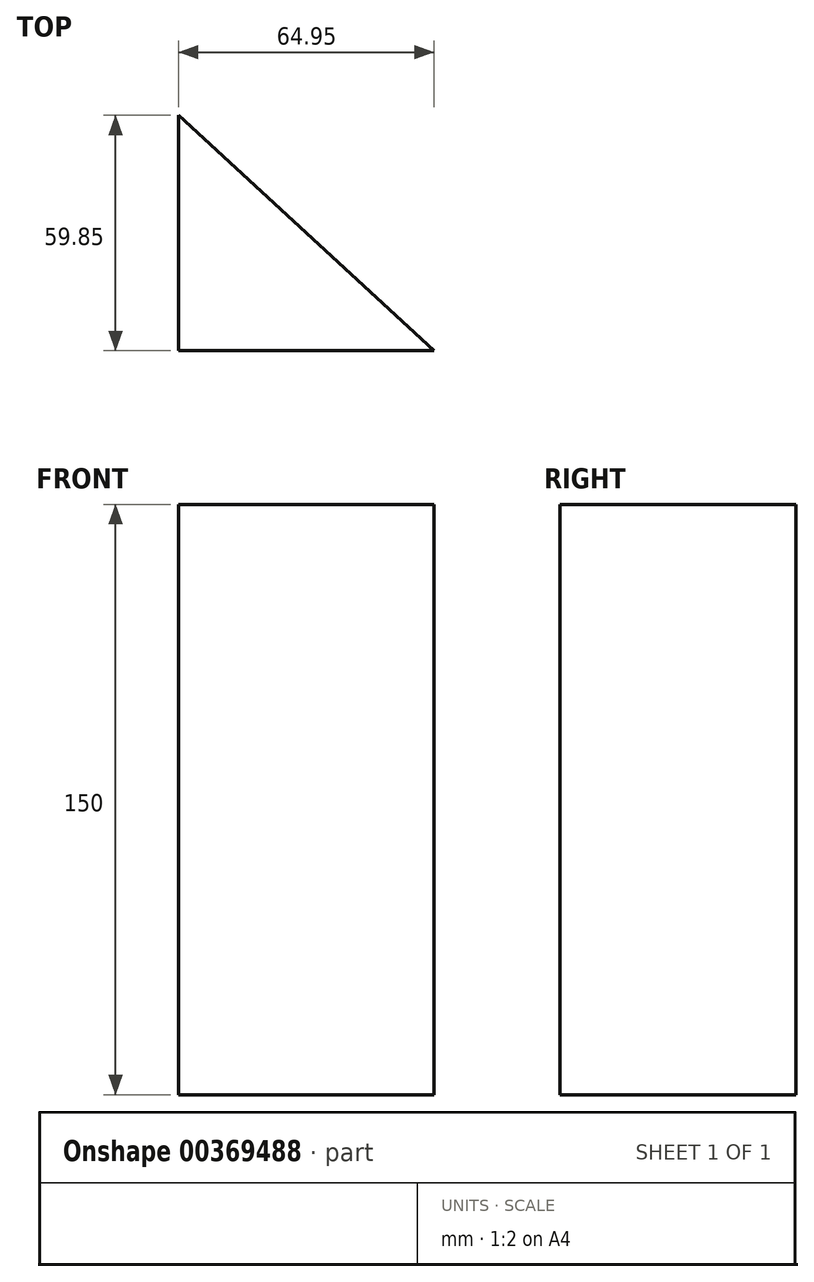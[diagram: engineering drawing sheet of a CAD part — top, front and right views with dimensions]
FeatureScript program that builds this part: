
annotation { "Feature Type Name" : "Feature", "Feature Type Description" : "" }
export const myFeature = defineFeature(function(context is Context, id is Id, definition is map)
    precondition{}
    {
        {
            var Q0;
            Q0=qCreatedBy(makeId("Top.planeOp"),FACE);
            var sketch = newSketch(context, id + "F0", { "sketchPlane" : qUnion([Q0])});
            skLineSegment(sketch, "E0", {"start": v(-31.8, 34.05) * mm, "end": v(-31.8, -25.8) * mm});
            skLineSegment(sketch, "E1", {"start": v(-31.8, -25.8) * mm, "end": v(33.15, -25.8) * mm});
            skLineSegment(sketch, "E2", {"start": v(-31.8, 34.05) * mm, "end": v(33.15, -25.8) * mm});
            skSolve(sketch);
        }
        {
            var Q0;
            Q0=makeQuery(id+"F0.imprint","IMPRINT",FACE,{"disambiguationData":[TD([[makeQuery(id+"F0.imprint","IMPRINT",EDGE,{"derivedFrom":sQuery(id+"F0.wireOp",EDGE,"E0")}),1.0]])]});
            extrude(context, id + "F1", {"entities" : qUnion([Q0]), "depth" : 150 * mm});
        }
    });
